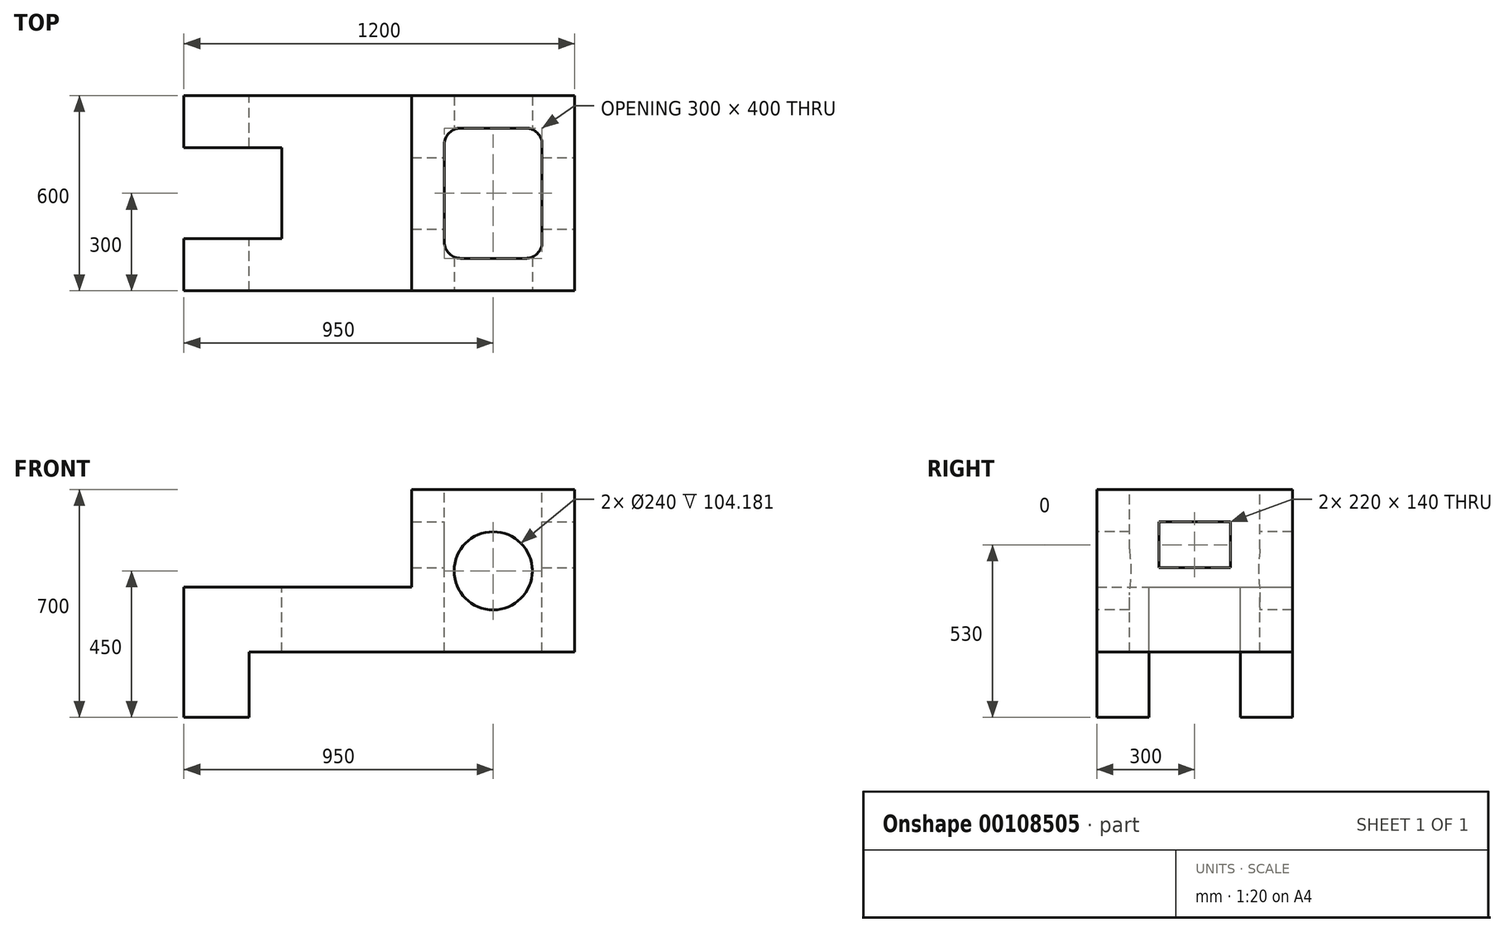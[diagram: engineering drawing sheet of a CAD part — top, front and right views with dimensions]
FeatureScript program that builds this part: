
annotation { "Feature Type Name" : "Feature", "Feature Type Description" : "" }
export const myFeature = defineFeature(function(context is Context, id is Id, definition is map)
    precondition{}
    {
        {
            var Q0;
            Q0=qCreatedBy(makeId("Front.planeOp"),FACE);
            var sketch = newSketch(context, id + "F0", { "sketchPlane" : qUnion([Q0])});
            skLineSegment(sketch, "E0", {"start": v(0, 0) * mm, "end": v(200, 0) * mm});
            skLineSegment(sketch, "E1", {"start": v(200, 0) * mm, "end": v(200, 200) * mm});
            skLineSegment(sketch, "E2", {"start": v(200, 200) * mm, "end": v(1200, 200) * mm});
            skLineSegment(sketch, "E3", {"start": v(1200, 200) * mm, "end": v(1200, 700) * mm});
            skLineSegment(sketch, "E4", {"start": v(1200, 700) * mm, "end": v(700, 700) * mm});
            skLineSegment(sketch, "E5", {"start": v(700, 700) * mm, "end": v(700, 400) * mm});
            skLineSegment(sketch, "E6", {"start": v(700, 400) * mm, "end": v(0, 400) * mm});
            skLineSegment(sketch, "E7", {"start": v(0, 400) * mm, "end": v(0, 0) * mm});
            skSolve(sketch);
        }
        {
            var Q0;
            Q0 = qSketchRegion(id + "F0", true);
            extrude(context, id + "F1", {"entities" : qUnion([Q0]), "depth" : 600 * mm});
        }
        {
            var Q0;
            Q0=makeQuery(id+"F1.opExtrude","SWEPT_FACE",FACE,{"disambiguationData":[OSD([sQuery(id+"F0.wireOp",EDGE,"E6")])]});
            var sketch = newSketch(context, id + "F2", { "sketchPlane" : qUnion([Q0])});
            skLineSegment(sketch, "E8.bottom", {"start": v(300, -440) * mm, "end": v(-300, -440) * mm});
            skLineSegment(sketch, "E8.top", {"start": v(300, -160) * mm, "end": v(-300, -160) * mm});
            skLineSegment(sketch, "E8.left", {"start": v(300, -440) * mm, "end": v(300, -160) * mm});
            skLineSegment(sketch, "E8.right", {"start": v(-300, -440) * mm, "end": v(-300, -160) * mm});
            skPoint(sketch, "E8.middle", {"position": v(0, -300) * mm});
            skSolve(sketch);
        }
        {
            var Q0;
            Q0 = qSketchRegion(id + "F2", true);
            extrude(context, id + "F3", {"entities" : qUnion([Q0]), "operationType" : NewBodyOperationType.REMOVE, "endBound" : BoundingType.THROUGH_ALL, "oppositeDirection" : true, "depth" : 25 * mm});
        }
        {
            var Q0;
            Q0=makeQuery(id+"F1.opExtrude","CAP_FACE",FACE,{"disambiguationData":[OSD([sQuery(id+"F0.wireOp",EDGE,"E0"),sQuery(id+"F0.wireOp",EDGE,"E1"),sQuery(id+"F0.wireOp",EDGE,"E2"),sQuery(id+"F0.wireOp",EDGE,"E3"),sQuery(id+"F0.wireOp",EDGE,"E4"),sQuery(id+"F0.wireOp",EDGE,"E5"),sQuery(id+"F0.wireOp",EDGE,"E6"),sQuery(id+"F0.wireOp",EDGE,"E7")])],"isStart":false});
            var sketch = newSketch(context, id + "F4", { "sketchPlane" : qUnion([Q0])});
            skLineSegment(sketch, "E9", {"start": v(1200, 450) * mm, "end": v(950, 450) * mm, "construction": true});
            skPoint(sketch, "E9.endSnap0", {"position": v(950, 700) * mm});
            skCircle(sketch, "E10", {"center": v(950, 450) * mm, "radius": 120 * mm});
            skSolve(sketch);
        }
        {
            var Q0;
            Q0 = qSketchRegion(id + "F4", true);
            extrude(context, id + "F5", {"entities" : qUnion([Q0]), "operationType" : NewBodyOperationType.REMOVE, "endBound" : BoundingType.THROUGH_ALL, "oppositeDirection" : true, "depth" : 25 * mm});
        }
        {
            var Q0;
            Q0=makeQuery(id+"F1.opExtrude","SWEPT_FACE",FACE,{"disambiguationData":[OSD([sQuery(id+"F0.wireOp",EDGE,"E4")])]});
            var sketch = newSketch(context, id + "F6", { "sketchPlane" : qUnion([Q0])});
            skLineSegment(sketch, "E11", {"start": v(1200, -300) * mm, "end": v(950, -300) * mm, "construction": true});
            skPoint(sketch, "E11.endSnap0", {"position": v(950, 0) * mm});
            skLineSegment(sketch, "E12.bottom", {"start": v(1050, -500) * mm, "end": v(850, -500) * mm});
            skLineSegment(sketch, "E12.top", {"start": v(1050, -100) * mm, "end": v(850, -100) * mm});
            skLineSegment(sketch, "E12.left", {"start": v(1100, -450) * mm, "end": v(1100, -150) * mm});
            skLineSegment(sketch, "E12.right", {"start": v(800, -450) * mm, "end": v(800, -150) * mm});
            skPoint(sketch, "E12.middle", {"position": v(950, -300) * mm});
            skPoint(sketch, "E13.visualSharp", {"position": v(800, -100) * mm});
            skArc(sketch, "E13.filletArc", {"start": v(850, -100) * mm, "mid": v(814.64, -114.64) * mm, "end": v(800, -150) * mm});
            skPoint(sketch, "E14.visualSharp", {"position": v(800, -500) * mm});
            skArc(sketch, "E14.filletArc", {"start": v(800, -450) * mm, "mid": v(814.64, -485.36) * mm, "end": v(850, -500) * mm});
            skPoint(sketch, "E15.visualSharp", {"position": v(1100, -500) * mm});
            skArc(sketch, "E15.filletArc", {"start": v(1050, -500) * mm, "mid": v(1085.36, -485.36) * mm, "end": v(1100, -450) * mm});
            skPoint(sketch, "E16.visualSharp", {"position": v(1100, -100) * mm});
            skArc(sketch, "E16.filletArc", {"start": v(1100, -150) * mm, "mid": v(1085.36, -114.64) * mm, "end": v(1050, -100) * mm});
            skSolve(sketch);
        }
        {
            var Q0;
            Q0 = qSketchRegion(id + "F6", true);
            extrude(context, id + "F7", {"entities" : qUnion([Q0]), "operationType" : NewBodyOperationType.REMOVE, "endBound" : BoundingType.THROUGH_ALL, "oppositeDirection" : true, "depth" : 25 * mm});
        }
        {
            var Q0;
            Q0=makeQuery(id+"F1.opExtrude","SWEPT_FACE",FACE,{"disambiguationData":[OSD([sQuery(id+"F0.wireOp",EDGE,"E3")])]});
            var sketch = newSketch(context, id + "F8", { "sketchPlane" : qUnion([Q0])});
            skLineSegment(sketch, "E17.bottom", {"start": v(-190, 460) * mm, "end": v(-410, 460) * mm});
            skLineSegment(sketch, "E17.top", {"start": v(-190, 600) * mm, "end": v(-410, 600) * mm});
            skLineSegment(sketch, "E17.left", {"start": v(-190, 460) * mm, "end": v(-190, 600) * mm});
            skLineSegment(sketch, "E17.right", {"start": v(-410, 460) * mm, "end": v(-410, 600) * mm});
            skPoint(sketch, "E17.middle", {"position": v(-300, 530) * mm});
            skPoint(sketch, "E17.middle.positionSnap0", {"position": v(-300, 700) * mm});
            skPoint(sketch, "E17.centerSnap0", {"position": v(-300, 700) * mm});
            skSolve(sketch);
        }
        {
            var Q0;
            Q0 = qSketchRegion(id + "F8", true);
            extrude(context, id + "F9", {"entities" : qUnion([Q0]), "operationType" : NewBodyOperationType.REMOVE, "endBound" : BoundingType.THROUGH_ALL, "oppositeDirection" : true, "depth" : 25 * mm});
        }
    });
